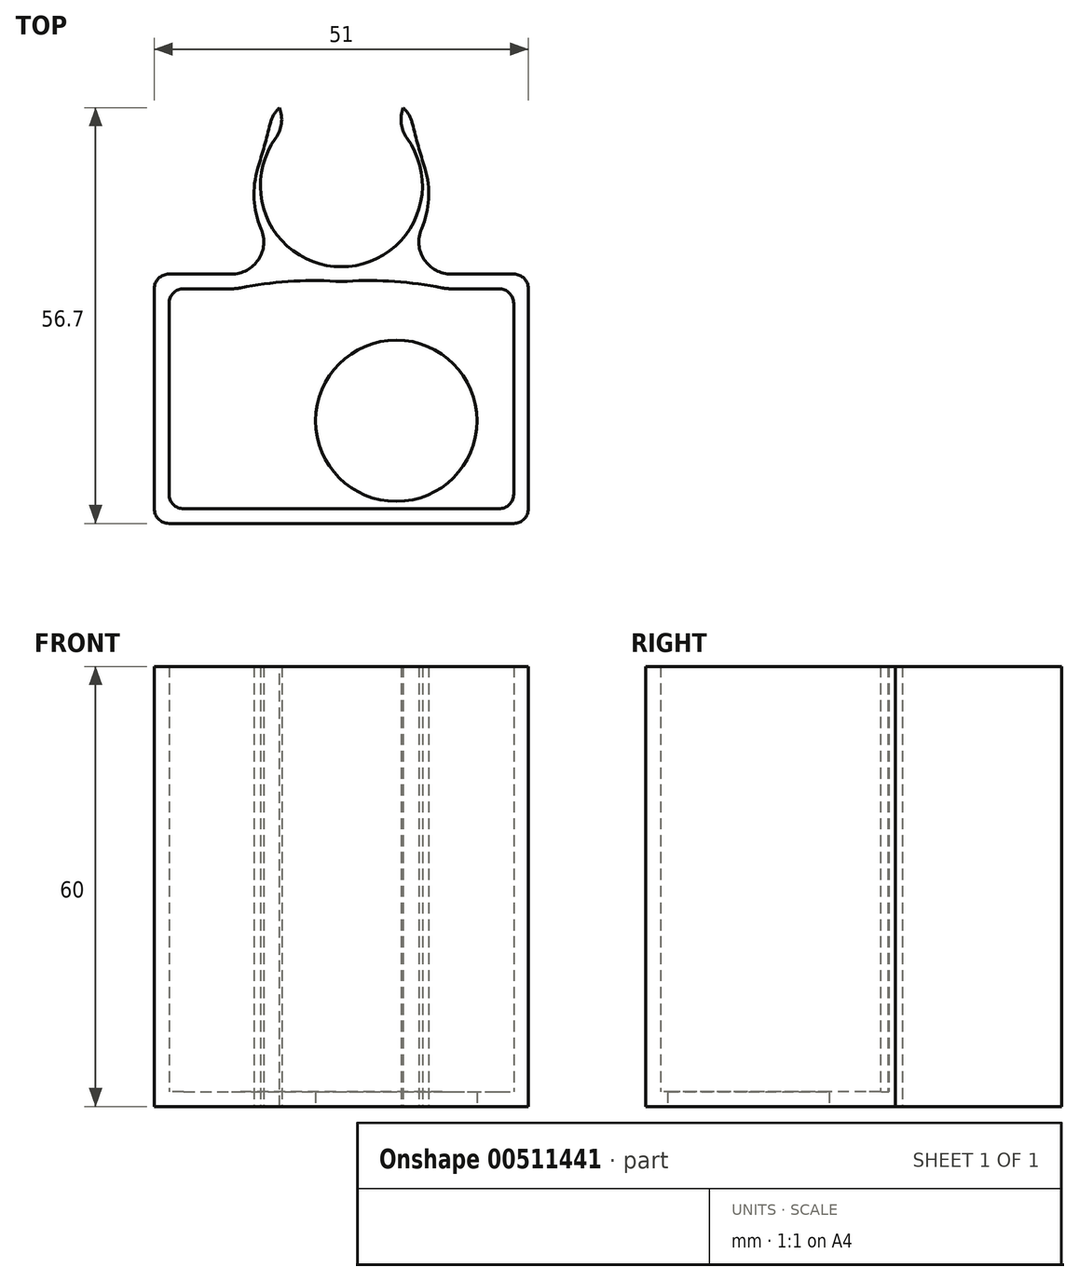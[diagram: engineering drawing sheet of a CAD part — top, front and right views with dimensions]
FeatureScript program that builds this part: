
annotation { "Feature Type Name" : "Feature", "Feature Type Description" : "" }
export const myFeature = defineFeature(function(context is Context, id is Id, definition is map)
    precondition{}
    {
        {
            assignVariable(context, id + "F0", {"variableType" : VariableType.LENGTH, "name" : "RodDiam", "lengthValue" : 22.1 * mm});
        }
        {
            assignVariable(context, id + "F1", {"variableType" : VariableType.LENGTH, "name" : "BaseThickness", "lengthValue" : 2 * mm});
        }
        {
            assignVariable(context, id + "F2", {"variableType" : VariableType.LENGTH, "name" : "BaseWidth", "lengthValue" : 51 * mm});
        }
        {
            assignVariable(context, id + "F3", {"variableType" : VariableType.LENGTH, "name" : "PocketHeight", "lengthValue" : 60 * mm});
        }
        {
            var Q0;
            Q0=qCreatedBy(makeId("Top.planeOp"),FACE);
            var sketch = newSketch(context, id + "F4", { "sketchPlane" : qUnion([Q0])});
            skLineSegment(sketch, "E0", {"start": v(0, 0) * mm, "end": v(0, 1) * mm, "construction": true});
            skLineSegment(sketch, "E1", {"start": v(0, 0) * mm, "end": v(0, -1) * mm, "construction": true});
            skLineSegment(sketch, "E2.bottom", {"start": v(-25.5, -2) * mm, "end": v(25.5, -2) * mm});
            skLineSegment(sketch, "E2.top", {"start": v(-25.5, 0) * mm, "end": v(25.5, 0) * mm});
            skLineSegment(sketch, "E2.left", {"start": v(-25.5, -2) * mm, "end": v(-25.5, 0) * mm});
            skLineSegment(sketch, "E2.right", {"start": v(25.5, -2) * mm, "end": v(25.5, 0) * mm});
            skPoint(sketch, "E2.middle", {"position": v(0, -1) * mm});
            skLineSegment(sketch, "E3", {"start": v(0, 1) * mm, "end": v(0, 12.05) * mm, "construction": true});
            skLineSegment(sketch, "E4", {"start": v(0, 12.05) * mm, "end": v(7.46, 20.2) * mm, "construction": true});
            skLineSegment(sketch, "E5", {"start": v(0, 1) * mm, "end": v(7.46, 20.2) * mm, "construction": true});
            skLineSegment(sketch, "E6.MirrorCS", {"start": v(0, 12.05) * mm, "end": v(-7.46, 20.2) * mm, "construction": true});
            skArc(sketch, "E7", {"start": v(-7.46, 20.2) * mm, "mid": v(0, 1) * mm, "end": v(7.46, 20.2) * mm});
            skArc(sketch, "E8", {"start": v(-7.46, 20.2) * mm, "mid": v(0, -1) * mm, "end": v(7.46, 20.2) * mm});
            skLineSegment(sketch, "E9", {"start": v(7.46, 20.2) * mm, "end": v(8.9, 23.93) * mm});
            skLineSegment(sketch, "E10", {"start": v(8.9, 23.93) * mm, "end": v(8.9, 18.82) * mm});
            skLineSegment(sketch, "E11.MirrorCS", {"start": v(-7.46, 20.2) * mm, "end": v(-8.9, 23.93) * mm});
            skLineSegment(sketch, "E12.MirrorCS", {"start": v(-8.9, 23.93) * mm, "end": v(-8.9, 18.82) * mm});
            skLineSegment(sketch, "E13.top", {"start": v(-25.5, -34) * mm, "end": v(25.5, -34) * mm});
            skLineSegment(sketch, "E13.left", {"start": v(-25.5, -2) * mm, "end": v(-25.5, -34) * mm});
            skLineSegment(sketch, "E13.right", {"start": v(25.5, -2) * mm, "end": v(25.5, -34) * mm});
            skSolve(sketch);
        }
        {
            var Q0;
            Q0=qSketchRegion(id+"F4",true);
            extrude(context, id + "F5", {"entities" : qUnion([Q0]), "depth" : getVariable(context, 'PocketHeight'), "offsetDistance" : 25 * mm});
        }
        {
            var Q0;
            Q0=makeQuery(id+"F5.opExtrude","SWEPT_EDGE",EDGE,{"disambiguationData":[OSD([sQuery(id+"F4.wireOp",EDGE,"E8"),sQuery(id+"F4.wireOp",EDGE,"E12.MirrorCS")])]});
            var Q1;
            Q1=makeQuery(id+"F5.opExtrude","SWEPT_EDGE",EDGE,{"disambiguationData":[OSD([sQuery(id+"F4.wireOp",EDGE,"E8"),sQuery(id+"F4.wireOp",EDGE,"E10")])]});
            fillet(context, id + "F6", {"entities" : qUnion([Q0, Q1]), "radius" : getVariable(context, 'RodDiam') * 5, "tangentPropagation" : true, "allowEdgeOverflow" : false});
        }
        {
            var Q0;
            {var subQ0=sQuery(id+"F4.wireOp",EDGE,"E8");var subQ1=sQuery(id+"F4.wireOp",EDGE,"E2.top");Q0=makeQuery(id+"F5.opExtrude","SWEPT_EDGE",EDGE,{"disambiguationData":[OSD([subQ1,subQ0]),TDD([makeQuery(id+"F4.imprint","INTERSECT",VERTEX,{"disambiguationData":[OD(0.0)],"derivedFrom":[subQ1,subQ0]})])]});}
            var Q1;
            {var subQ0=sQuery(id+"F4.wireOp",EDGE,"E8");var subQ1=sQuery(id+"F4.wireOp",EDGE,"E2.top");Q1=makeQuery(id+"F5.opExtrude","SWEPT_EDGE",EDGE,{"disambiguationData":[OSD([subQ1,subQ0]),TDD([makeQuery(id+"F4.imprint","INTERSECT",VERTEX,{"disambiguationData":[OD(1.0)],"derivedFrom":[subQ1,subQ0]})])]});}
            fillet(context, id + "F7", {"entities" : qUnion([Q0, Q1]), "radius" : getVariable(context, 'RodDiam') / 5, "tangentPropagation" : true, "allowEdgeOverflow" : false});
        }
        {
            var Q0;
            Q0=makeQuery(id+"F5.opExtrude","SWEPT_EDGE",EDGE,{"disambiguationData":[OSD([sQuery(id+"F4.wireOp",EDGE,"E7"),sQuery(id+"F4.wireOp",EDGE,"E8"),sQuery(id+"F4.wireOp",EDGE,"E9")])]});
            var Q1;
            Q1=makeQuery(id+"F5.opExtrude","SWEPT_EDGE",EDGE,{"disambiguationData":[OSD([sQuery(id+"F4.wireOp",EDGE,"E7"),sQuery(id+"F4.wireOp",EDGE,"E8"),sQuery(id+"F4.wireOp",EDGE,"E11.MirrorCS")])]});
            fillet(context, id + "F8", {"entities" : qUnion([Q0, Q1]), "radius" : getVariable(context, 'RodDiam') / 5, "tangentPropagation" : true, "allowEdgeOverflow" : false});
        }
        {
            var Q0;
            Q0=makeQuery(id+"F6.opFillet","BLEND_EDGE",EDGE,{"blendedFrom":[makeQuery(id+"F5.opExtrude","SWEPT_EDGE",EDGE,{"disambiguationData":[OSD([sQuery(id+"F4.wireOp",EDGE,"E8"),sQuery(id+"F4.wireOp",EDGE,"E10")])]}),makeQuery(id+"F5.opExtrude","SWEPT_FACE",FACE,{"disambiguationData":[OSD([sQuery(id+"F4.wireOp",EDGE,"E9")])]})],"blendedInto":[makeQuery(id+"F5.opExtrude","SWEPT_FACE",FACE,{"disambiguationData":[OSD([sQuery(id+"F4.wireOp",EDGE,"E9")])]})]});
            var Q1;
            Q1=makeQuery(id+"F6.opFillet","BLEND_EDGE",EDGE,{"blendedFrom":[makeQuery(id+"F5.opExtrude","SWEPT_EDGE",EDGE,{"disambiguationData":[OSD([sQuery(id+"F4.wireOp",EDGE,"E8"),sQuery(id+"F4.wireOp",EDGE,"E12.MirrorCS")])]}),makeQuery(id+"F5.opExtrude","SWEPT_FACE",FACE,{"disambiguationData":[OSD([sQuery(id+"F4.wireOp",EDGE,"E11.MirrorCS")])]})],"blendedInto":[makeQuery(id+"F5.opExtrude","SWEPT_FACE",FACE,{"disambiguationData":[OSD([sQuery(id+"F4.wireOp",EDGE,"E11.MirrorCS")])]})]});
            fillet(context, id + "F9", {"entities" : qUnion([Q0, Q1]), "radius" : getVariable(context, 'RodDiam') / 5, "tangentPropagation" : true, "allowEdgeOverflow" : false});
        }
        {
            var Q0;
            Q0=makeQuery(id+"F5.opExtrude","CAP_FACE",FACE,{"disambiguationData":[OSD([sQuery(id+"F4.wireOp",EDGE,"E2.top"),sQuery(id+"F4.wireOp",EDGE,"E2.left"),sQuery(id+"F4.wireOp",EDGE,"E2.right"),sQuery(id+"F4.wireOp",EDGE,"E7"),sQuery(id+"F4.wireOp",EDGE,"E8"),sQuery(id+"F4.wireOp",EDGE,"E9"),sQuery(id+"F4.wireOp",EDGE,"E10"),sQuery(id+"F4.wireOp",EDGE,"E11.MirrorCS"),sQuery(id+"F4.wireOp",EDGE,"E12.MirrorCS"),sQuery(id+"F4.wireOp",EDGE,"E13.top"),sQuery(id+"F4.wireOp",EDGE,"E13.left"),sQuery(id+"F4.wireOp",EDGE,"E13.right")])],"isStart":false});
            shell(context, id + "F10", {"entities" : qUnion([Q0]), "thickness" : 2 * mm});
        }
        {
            var Q0;
            Q0=makeQuery(id+"F5.opExtrude","CAP_FACE",FACE,{"disambiguationData":[OSD([sQuery(id+"F4.wireOp",EDGE,"E2.top"),sQuery(id+"F4.wireOp",EDGE,"E2.left"),sQuery(id+"F4.wireOp",EDGE,"E2.right"),sQuery(id+"F4.wireOp",EDGE,"E7"),sQuery(id+"F4.wireOp",EDGE,"E8"),sQuery(id+"F4.wireOp",EDGE,"E9"),sQuery(id+"F4.wireOp",EDGE,"E10"),sQuery(id+"F4.wireOp",EDGE,"E11.MirrorCS"),sQuery(id+"F4.wireOp",EDGE,"E12.MirrorCS"),sQuery(id+"F4.wireOp",EDGE,"E13.top"),sQuery(id+"F4.wireOp",EDGE,"E13.left"),sQuery(id+"F4.wireOp",EDGE,"E13.right")])],"isStart":true});
            var sketch = newSketch(context, id + "F11", { "sketchPlane" : qUnion([Q0])});
            skLineSegment(sketch, "E14", {"start": v(25.5, 20) * mm, "end": v(7.5, 20) * mm, "construction": true});
            skCircle(sketch, "E15", {"center": v(7.5, 20) * mm, "radius": 11 * mm});
            skLineSegment(sketch, "E16", {"start": v(25.5, 0) * mm, "end": v(25.5, 20) * mm, "construction": true});
            skSolve(sketch);
        }
        {
            var Q0;
            Q0=makeQuery(id+"F11.imprint","IMPRINT",FACE,{"disambiguationData":[TD([[makeQuery(id+"F11.imprint","IMPRINT",EDGE,{"derivedFrom":sQuery(id+"F11.wireOp",EDGE,"E15")}),1.0]])]});
            extrude(context, id + "F12", {"entities" : qUnion([Q0]), "operationType" : NewBodyOperationType.REMOVE, "oppositeDirection" : true, "depth" : getVariable(context, 'BaseThickness'), "offsetDistance" : 25 * mm});
        }
        {
            var Q0;
            {var subQ0=sQuery(id+"F4.wireOp",EDGE,"E8");var subQ1=sQuery(id+"F4.wireOp",EDGE,"E2.top");Q0=makeQuery(id+"F10.opShell","TWEAK_EDGE",EDGE,{"derivedFrom":[makeQuery(id+"F7.opFillet","BLEND_FACE",FACE,{"disambiguationData":[OSD([subQ1,subQ0]),TDD([makeQuery(id+"F5.opExtrude","SWEPT_EDGE",EDGE,{"disambiguationData":[OSD([subQ1,subQ0]),TDD([makeQuery(id+"F4.imprint","INTERSECT",VERTEX,{"disambiguationData":[OD(1.0)],"derivedFrom":[subQ1,subQ0]})])]})])]}),makeQuery(id+"F5.opExtrude","SWEPT_FACE",FACE,{"disambiguationData":[OSD([sQuery(id+"F4.wireOp",EDGE,"E7")])]})]});}
            var Q1;
            {var subQ0=sQuery(id+"F4.wireOp",EDGE,"E8");var subQ1=sQuery(id+"F4.wireOp",EDGE,"E2.top");Q1=makeQuery(id+"F10.opShell","TWEAK_EDGE",EDGE,{"derivedFrom":[makeQuery(id+"F7.opFillet","BLEND_FACE",FACE,{"disambiguationData":[OSD([subQ1,subQ0]),TDD([makeQuery(id+"F5.opExtrude","SWEPT_EDGE",EDGE,{"disambiguationData":[OSD([subQ1,subQ0]),TDD([makeQuery(id+"F4.imprint","INTERSECT",VERTEX,{"disambiguationData":[OD(0.0)],"derivedFrom":[subQ1,subQ0]})])]})])]}),makeQuery(id+"F5.opExtrude","SWEPT_FACE",FACE,{"disambiguationData":[OSD([sQuery(id+"F4.wireOp",EDGE,"E7")])]})]});}
            fillet(context, id + "F13", {"entities" : qUnion([Q0, Q1]), "radius" : getVariable(context, 'BaseWidth'), "tangentPropagation" : true, "allowEdgeOverflow" : false});
        }
        {
            var Q0;
            Q0=makeQuery(id+"F5.opExtrude","SWEPT_EDGE",EDGE,{"disambiguationData":[OSD([sQuery(id+"F4.wireOp",EDGE,"E2.top"),sQuery(id+"F4.wireOp",EDGE,"E2.left")])]});
            var Q1;
            Q1=makeQuery(id+"F5.opExtrude","SWEPT_EDGE",EDGE,{"disambiguationData":[OSD([sQuery(id+"F4.wireOp",EDGE,"E2.top"),sQuery(id+"F4.wireOp",EDGE,"E2.right")])]});
            var Q2;
            Q2=makeQuery(id+"F10.opShell","OFFSET_EDGE",EDGE,{"disambiguationData":[OSD([sQuery(id+"F4.wireOp",EDGE,"E13.top"),sQuery(id+"F4.wireOp",EDGE,"E13.right")])]});
            var Q3;
            Q3=makeQuery(id+"F10.opShell","OFFSET_EDGE",EDGE,{"disambiguationData":[OSD([sQuery(id+"F4.wireOp",EDGE,"E13.top"),sQuery(id+"F4.wireOp",EDGE,"E13.left")])]});
            var Q4;
            Q4=makeQuery(id+"F5.opExtrude","SWEPT_EDGE",EDGE,{"disambiguationData":[OSD([sQuery(id+"F4.wireOp",EDGE,"E13.top"),sQuery(id+"F4.wireOp",EDGE,"E13.right")])]});
            var Q5;
            Q5=makeQuery(id+"F5.opExtrude","SWEPT_EDGE",EDGE,{"disambiguationData":[OSD([sQuery(id+"F4.wireOp",EDGE,"E13.top"),sQuery(id+"F4.wireOp",EDGE,"E13.left")])]});
            var Q6;
            Q6=makeQuery(id+"F10.opShell","OFFSET_EDGE",EDGE,{"disambiguationData":[OSD([sQuery(id+"F4.wireOp",EDGE,"E2.top"),sQuery(id+"F4.wireOp",EDGE,"E2.right")])]});
            var Q7;
            Q7=makeQuery(id+"F10.opShell","OFFSET_EDGE",EDGE,{"disambiguationData":[OSD([sQuery(id+"F4.wireOp",EDGE,"E2.top"),sQuery(id+"F4.wireOp",EDGE,"E2.left")])]});
            fillet(context, id + "F14", {"entities" : qUnion([Q0, Q1, Q2, Q3, Q4, Q5, Q6, Q7]), "radius" : getVariable(context, 'BaseThickness'), "tangentPropagation" : true, "allowEdgeOverflow" : false});
        }
    });
